# Revit family: DOOR_2P_1HD_1A_1F
name_source: partatom
category: Doors
units: mm (PartAtom-declared; Revit-internal decimal feet)

## family parameters
Always vertical = Yes
Cut with Voids When Loaded = Yes
Host = Wall
OmniClass Number = 23.30.10.00
OmniClass Title = Doors
Room Calculation Point = No
Shared = No

## types (2) — shared parameters
APL Frame = <By Category>
Analytic Construction = <None>
Architrave = Yes
Architrave Length = 40 mm  [stored 0.131234 ft]
Architrave Thickness = 10 mm  [stored 0.0328084 ft]
Construction Type = 641
Define Thermal Properties by = Schematic Type
Function = Exterior
Glass = <By Category>
Height = 2190 mm  [stored 7.18504 ft]
Hinged Door Width = 930 mm
OSB Film = OSB Film
Rebate = 35 mm  [stored 0.114829 ft]
Rough Height = 2210 mm  [stored 7.25066 ft]
Rough Width = 1920 mm  [stored 6.29921 ft]
Timber Jamb = 20 mm  [stored 0.0656168 ft]
Timber Jamb Length = 110 mm  [stored 0.360892 ft]
Timber Jamb at Sill = No
Timber Packer = 10 mm  [stored 0.0328084 ft]
Transom Height Door = 740 mm  [stored 2.42782 ft]
Transom Height Glass Panel = 1822 mm  [stored 5.97769 ft]
Void Depth = 150 mm  [stored 0.492126 ft]
Void Head Height = 2330 mm  [stored 7.64436 ft]
Void Sill Height = -120 mm  [stored -0.393701 ft]
Void Width Right = 20 mm  [stored 0.0656168 ft]
Void Width left = 20 mm  [stored 0.0656168 ft]
Wall Closure = By host
Width = 1900 mm  [stored 6.2336 ft]

## per-type parameters (varying)
| type | Door Left Side | Door Right Side |
| 1900w x 2190h_DR Left Side | Yes | No |
| 1900w x 2190h_DR Right Side | No | Yes |

note: [stored X ft] marks values corroborated as IEEE doubles in the binary element streams (Revit-internal decimal feet)

## geometry (parser evidence)
native form markers: Sweep x29
no freeform markers — native parametric forms only
